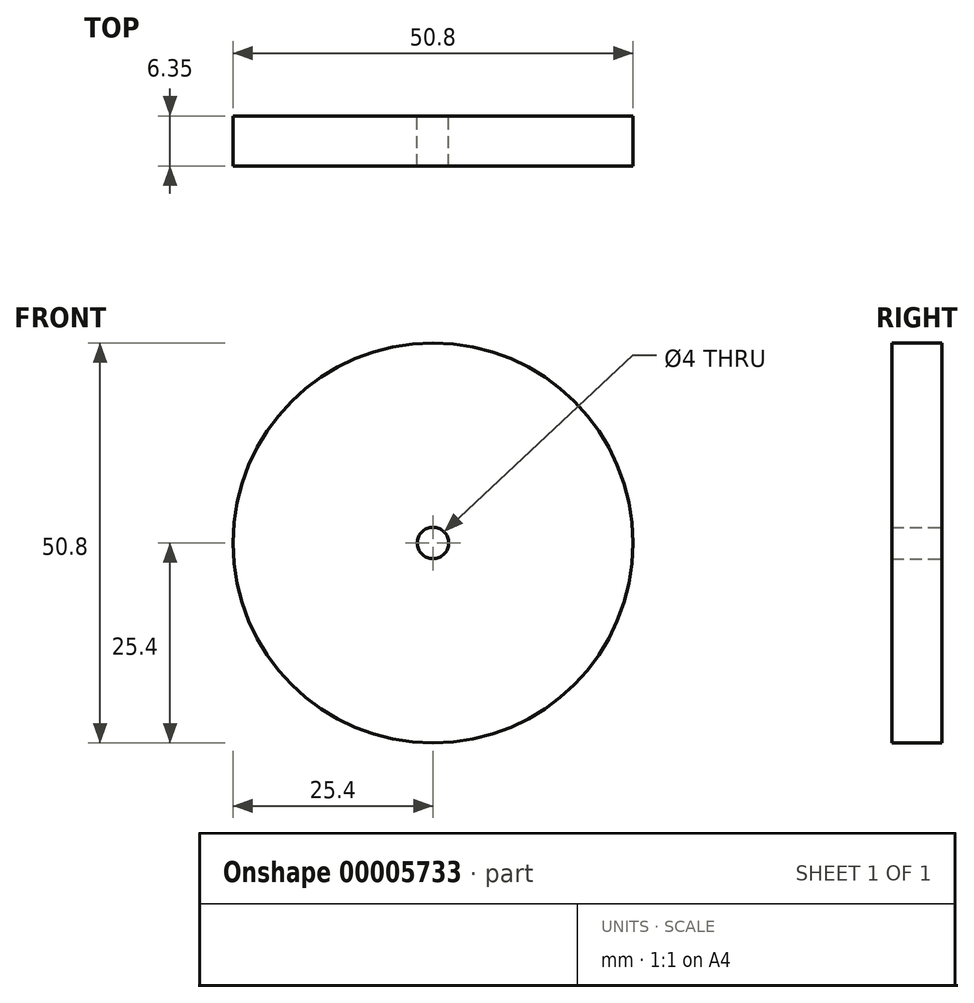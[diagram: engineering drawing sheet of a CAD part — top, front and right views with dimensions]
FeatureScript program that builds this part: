
annotation { "Feature Type Name" : "Feature", "Feature Type Description" : "" }
export const myFeature = defineFeature(function(context is Context, id is Id, definition is map)
    precondition{}
    {
        {
            var Q0;
            Q0=qCreatedBy(makeId("Front.planeOp"),FACE);
            var sketch = newSketch(context, id + "F0", { "sketchPlane" : qUnion([Q0])});
            skCircle(sketch, "E0", {"center": v(0, 0) * mm, "radius": 25.4 * mm});
            skCircle(sketch, "E1", {"center": v(0, 0) * mm, "radius": 2 * mm});
            skSolve(sketch);
        }
        {
            var Q0;
            Q0 = qSketchRegion(id + "F0", true);
            extrude(context, id + "F1", {"entities" : qUnion([Q0]), "depth" : 6.35 * mm});
        }
    });
